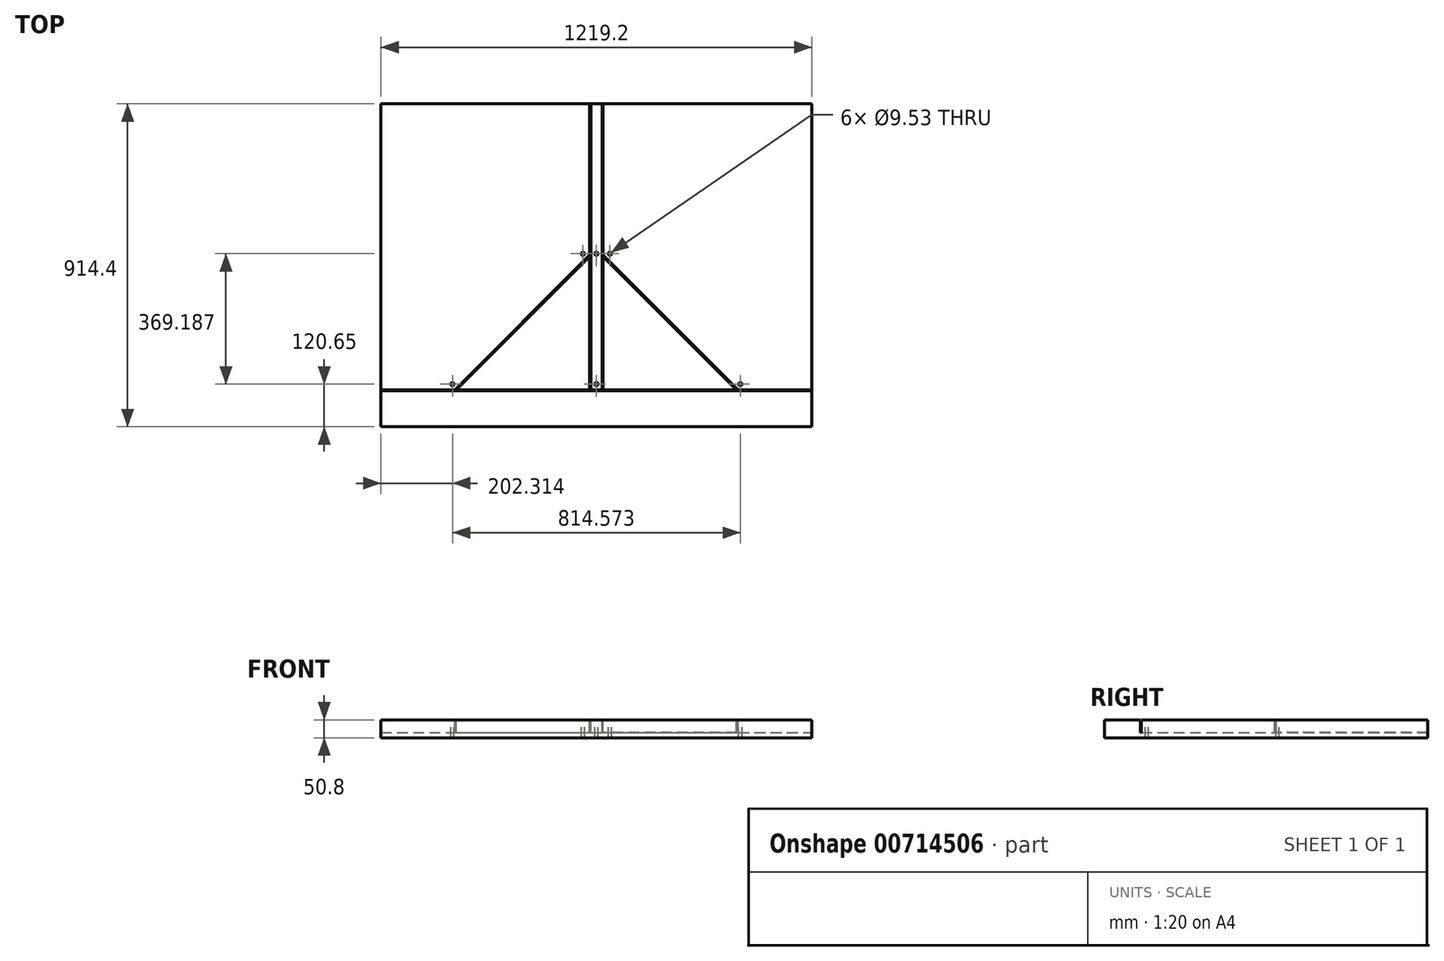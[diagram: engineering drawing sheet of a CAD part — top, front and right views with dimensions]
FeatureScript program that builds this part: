
annotation { "Feature Type Name" : "Feature", "Feature Type Description" : "" }
export const myFeature = defineFeature(function(context is Context, id is Id, definition is map)
    precondition{}
    {
        {
            var Q0;
            Q0=qCreatedBy(makeId("Top.planeOp"),FACE);
            var sketch = newSketch(context, id + "F0", { "sketchPlane" : qUnion([Q0])});
            skLineSegment(sketch, "E0.bottom", {"start": v(0, 0) * mm, "end": v(1219.2, 0) * mm});
            skLineSegment(sketch, "E0.top", {"start": v(0, 914.4) * mm, "end": v(1219.2, 914.4) * mm});
            skLineSegment(sketch, "E0.left", {"start": v(0, 0) * mm, "end": v(0, 914.4) * mm});
            skLineSegment(sketch, "E0.right", {"start": v(1219.2, 0) * mm, "end": v(1219.2, 914.4) * mm});
            skSolve(sketch);
        }
        {
            var Q0;
            Q0=makeQuery(id+"F0.imprint","IMPRINT",FACE,{"disambiguationData":[TD([[makeQuery(id+"F0.imprint","IMPRINT",EDGE,{"derivedFrom":sQuery(id+"F0.wireOp",EDGE,"E0.bottom")}),1.0]])]});
            extrude(context, id + "F1", {"entities" : qUnion([Q0]), "depth" : 50.8 * mm, "offsetDistance" : 25.4 * mm});
        }
        {
            var Q0;
            Q0=makeQuery(id+"F1.opExtrude","CAP_FACE",FACE,{"disambiguationData":[OSD([sQuery(id+"F0.wireOp",EDGE,"E0.bottom"),sQuery(id+"F0.wireOp",EDGE,"E0.top"),sQuery(id+"F0.wireOp",EDGE,"E0.left"),sQuery(id+"F0.wireOp",EDGE,"E0.right")])],"isStart":false});
            var sketch = newSketch(context, id + "F2", { "sketchPlane" : qUnion([Q0])});
            skLineSegment(sketch, "E1.bottom", {"start": v(0, 101.6) * mm, "end": v(1219.2, 101.6) * mm});
            skLineSegment(sketch, "E1.top", {"start": v(0, 139.7) * mm, "end": v(1219.2, 139.7) * mm});
            skLineSegment(sketch, "E2", {"start": v(609.6, 101.6) * mm, "end": v(609.6, 139.7) * mm, "construction": true});
            skLineSegment(sketch, "E3", {"start": v(0, 104.78) * mm, "end": v(1219.2, 104.78) * mm});
            skPoint(sketch, "E3.endSnap0", {"position": v(1219.2, 120.65) * mm});
            skLineSegment(sketch, "E4", {"start": v(628.65, 104.78) * mm, "end": v(628.65, 1933.58) * mm});
            skLineSegment(sketch, "E5", {"start": v(628.65, 1933.58) * mm, "end": v(590.55, 1933.58) * mm});
            skLineSegment(sketch, "E6", {"start": v(590.55, 1933.58) * mm, "end": v(590.55, 104.78) * mm});
            skLineSegment(sketch, "E7", {"start": v(593.73, 104.78) * mm, "end": v(593.73, 1933.58) * mm});
            skLineSegment(sketch, "E8", {"start": v(213.38, 104.78) * mm, "end": v(590.55, 481.95) * mm});
            skLineSegment(sketch, "E9", {"start": v(590.55, 535.83) * mm, "end": v(159.5, 104.78) * mm});
            skLineSegment(sketch, "E10", {"start": v(1005.82, 104.78) * mm, "end": v(628.65, 481.95) * mm});
            skLineSegment(sketch, "E11", {"start": v(628.65, 535.83) * mm, "end": v(1059.7, 104.78) * mm});
            skLineSegment(sketch, "E12", {"start": v(208.89, 104.78) * mm, "end": v(590.55, 486.44) * mm});
            skLineSegment(sketch, "E13", {"start": v(628.65, 486.44) * mm, "end": v(1010.31, 104.78) * mm});
            skLineSegment(sketch, "E14", {"start": v(625.48, 104.78) * mm, "end": v(625.47, 1933.58) * mm});
            skSolve(sketch);
        }
        {
            var Q0;
            {var subQ0=sQuery(id+"F2.wireOp",EDGE,"E12");var subQ1=sQuery(id+"F2.wireOp",EDGE,"E1.top");var subQ2=makeQuery(id+"F2.imprint","INTERSECT",VERTEX,{"derivedFrom":[subQ1,subQ0]});Q0=makeQuery(id+"F2.imprint","IMPRINT",FACE,{"disambiguationData":[TD([[makeQuery(id+"F2.imprint","IMPRINT",EDGE,{"disambiguationData":[TD([[subQ2,-1.0]])],"derivedFrom":subQ1}),1.0]])]});}
            var Q1;
            {var subQ0=sQuery(id+"F2.wireOp",EDGE,"E6");var subQ6=sQuery(id+"F2.wireOp",EDGE,"E1.top");var subQ7=makeQuery(id+"F2.imprint","INTERSECT",VERTEX,{"derivedFrom":[subQ6,subQ0]});Q1=makeQuery(id+"F2.imprint","IMPRINT",FACE,{"disambiguationData":[TD([[makeQuery(id+"F2.imprint","IMPRINT",EDGE,{"disambiguationData":[TD([[subQ7,-1.0]])],"derivedFrom":subQ6}),1.0]])]});}
            var Q2;
            {var subQ0=sQuery(id+"F2.wireOp",EDGE,"E10");var subQ1=sQuery(id+"F2.wireOp",EDGE,"E1.top");var subQ2=makeQuery(id+"F2.imprint","INTERSECT",VERTEX,{"derivedFrom":[subQ1,subQ0]});Q2=makeQuery(id+"F2.imprint","IMPRINT",FACE,{"disambiguationData":[TD([[makeQuery(id+"F2.imprint","IMPRINT",EDGE,{"disambiguationData":[TD([[subQ2,-1.0]])],"derivedFrom":subQ1}),1.0]])]});}
            var Q3;
            {var subQ0=sQuery(id+"F2.wireOp",EDGE,"E6");var subQ1=sQuery(id+"F2.wireOp",EDGE,"E1.top");var subQ2=makeQuery(id+"F2.imprint","INTERSECT",VERTEX,{"derivedFrom":[subQ1,subQ0]});Q3=makeQuery(id+"F2.imprint","IMPRINT",FACE,{"disambiguationData":[TD([[makeQuery(id+"F2.imprint","IMPRINT",EDGE,{"disambiguationData":[TD([[subQ2,-1.0]])],"derivedFrom":subQ1}),-1.0]])]});}
            var Q4;
            {var subQ10=sQuery(id+"F2.wireOp",EDGE,"E1.bottom");Q4=makeQuery(id+"F2.imprint","IMPRINT",FACE,{"disambiguationData":[TD([[makeQuery(id+"F2.imprint","IMPRINT",EDGE,{"derivedFrom":subQ10}),1.0]])]});}
            var Q5;
            {var subQ0=sQuery(id+"F2.wireOp",EDGE,"E12");var subQ1=sQuery(id+"F2.wireOp",EDGE,"E1.top");var subQ2=makeQuery(id+"F2.imprint","INTERSECT",VERTEX,{"derivedFrom":[subQ1,subQ0]});Q5=makeQuery(id+"F2.imprint","IMPRINT",FACE,{"disambiguationData":[TD([[makeQuery(id+"F2.imprint","IMPRINT",EDGE,{"disambiguationData":[TD([[subQ2,-1.0]])],"derivedFrom":subQ1}),-1.0]])]});}
            var Q6;
            {var subQ0=sQuery(id+"F2.wireOp",EDGE,"E10");var subQ1=sQuery(id+"F2.wireOp",EDGE,"E1.top");var subQ2=makeQuery(id+"F2.imprint","INTERSECT",VERTEX,{"derivedFrom":[subQ1,subQ0]});Q6=makeQuery(id+"F2.imprint","IMPRINT",FACE,{"disambiguationData":[TD([[makeQuery(id+"F2.imprint","IMPRINT",EDGE,{"disambiguationData":[TD([[subQ2,-1.0]])],"derivedFrom":subQ1}),-1.0]])]});}
            var Q7;
            {var subQ4=sQuery(id+"F2.wireOp",EDGE,"E14");var subQ5=sQuery(id+"F2.wireOp",EDGE,"E1.top");var subQ6=makeQuery(id+"F2.imprint","INTERSECT",VERTEX,{"derivedFrom":[subQ5,subQ4]});Q7=makeQuery(id+"F2.imprint","IMPRINT",FACE,{"disambiguationData":[TD([[makeQuery(id+"F2.imprint","IMPRINT",EDGE,{"disambiguationData":[TD([[subQ6,-1.0]])],"derivedFrom":subQ5}),1.0]])]});}
            var Q8;
            {var subQ0=sQuery(id+"F2.wireOp",EDGE,"E14");var subQ1=sQuery(id+"F2.wireOp",EDGE,"E1.top");var subQ2=makeQuery(id+"F2.imprint","INTERSECT",VERTEX,{"derivedFrom":[subQ1,subQ0]});Q8=makeQuery(id+"F2.imprint","IMPRINT",FACE,{"disambiguationData":[TD([[makeQuery(id+"F2.imprint","IMPRINT",EDGE,{"disambiguationData":[TD([[subQ2,-1.0]])],"derivedFrom":subQ1}),-1.0]])]});}
            extrude(context, id + "F3", {"entities" : qUnion([Q0, Q1, Q2, Q3, Q4, Q5, Q6, Q7, Q8]), "operationType" : NewBodyOperationType.REMOVE, "oppositeDirection" : true, "depth" : 35.56 * mm, "offsetDistance" : 25.4 * mm});
        }
        {
            var Q0;
            {var subQ3=sQuery(id+"F2.wireOp",EDGE,"E12");var subQ4=sQuery(id+"F0.wireOp",EDGE,"E0.left");var subQ7=sQuery(id+"F0.wireOp",EDGE,"E0.top");Q0=makeQuery(id+"F3.boolean.opBoolean","SPLIT",FACE,{"disambiguationData":[TD([makeQuery(id+"F3.opExtrude","SWEPT_FACE",FACE,{"disambiguationData":[OSD([subQ3])]})])],"derivedFrom":makeQuery(id+"F1.opExtrude","CAP_FACE",FACE,{"disambiguationData":[OSD([sQuery(id+"F0.wireOp",EDGE,"E0.bottom"),subQ7,subQ4,sQuery(id+"F0.wireOp",EDGE,"E0.right")])],"isStart":false})});}
            var sketch = newSketch(context, id + "F4", { "sketchPlane" : qUnion([Q0])});
            skCircle(sketch, "E15", {"center": v(571.5, 489.84) * mm, "radius": 4.76 * mm});
            skCircle(sketch, "E16", {"center": v(609.6, 489.84) * mm, "radius": 4.76 * mm});
            skCircle(sketch, "E17", {"center": v(647.7, 489.84) * mm, "radius": 4.76 * mm});
            skCircle(sketch, "E18", {"center": v(202.31, 120.65) * mm, "radius": 4.76 * mm});
            skCircle(sketch, "E19", {"center": v(609.6, 120.65) * mm, "radius": 4.76 * mm});
            skCircle(sketch, "E20", {"center": v(1016.89, 120.65) * mm, "radius": 4.76 * mm});
            skLineSegment(sketch, "E21.0.0", {"start": v(1219.2, 101.6) * mm, "end": v(0, 101.6) * mm});
            skLineSegment(sketch, "E21.0.1", {"start": v(0, 101.6) * mm, "end": v(0, 0) * mm});
            skLineSegment(sketch, "E21.0.2", {"start": v(0, 0) * mm, "end": v(1219.2, 0) * mm});
            skLineSegment(sketch, "E21.0.3", {"start": v(1219.2, 0) * mm, "end": v(1219.2, 101.6) * mm});
            skSolve(sketch);
        }
        {
            var Q0;
            Q0=makeQuery(id+"F4.imprint","IMPRINT",FACE,{"disambiguationData":[TD([[makeQuery(id+"F4.imprint","IMPRINT",EDGE,{"derivedFrom":sQuery(id+"F4.wireOp",EDGE,"E18")}),1.0]])]});
            var Q1;
            Q1=makeQuery(id+"F4.imprint","IMPRINT",FACE,{"disambiguationData":[TD([[makeQuery(id+"F4.imprint","IMPRINT",EDGE,{"derivedFrom":sQuery(id+"F4.wireOp",EDGE,"E15")}),1.0]])]});
            var Q2;
            Q2=makeQuery(id+"F4.imprint","IMPRINT",FACE,{"disambiguationData":[TD([[makeQuery(id+"F4.imprint","IMPRINT",EDGE,{"derivedFrom":sQuery(id+"F4.wireOp",EDGE,"E16")}),1.0]])]});
            var Q3;
            Q3=makeQuery(id+"F4.imprint","IMPRINT",FACE,{"disambiguationData":[TD([[makeQuery(id+"F4.imprint","IMPRINT",EDGE,{"derivedFrom":sQuery(id+"F4.wireOp",EDGE,"E17")}),1.0]])]});
            var Q4;
            Q4=makeQuery(id+"F4.imprint","IMPRINT",FACE,{"disambiguationData":[TD([[makeQuery(id+"F4.imprint","IMPRINT",EDGE,{"derivedFrom":sQuery(id+"F4.wireOp",EDGE,"E19")}),1.0]])]});
            var Q5;
            Q5=makeQuery(id+"F4.imprint","IMPRINT",FACE,{"disambiguationData":[TD([[makeQuery(id+"F4.imprint","IMPRINT",EDGE,{"derivedFrom":sQuery(id+"F4.wireOp",EDGE,"E20")}),1.0]])]});
            extrude(context, id + "F5", {"entities" : qUnion([Q0, Q1, Q2, Q3, Q4, Q5]), "operationType" : NewBodyOperationType.REMOVE, "endBound" : BoundingType.THROUGH_ALL, "oppositeDirection" : true, "depth" : 25.4 * mm, "offsetDistance" : 25.4 * mm});
        }
    });
